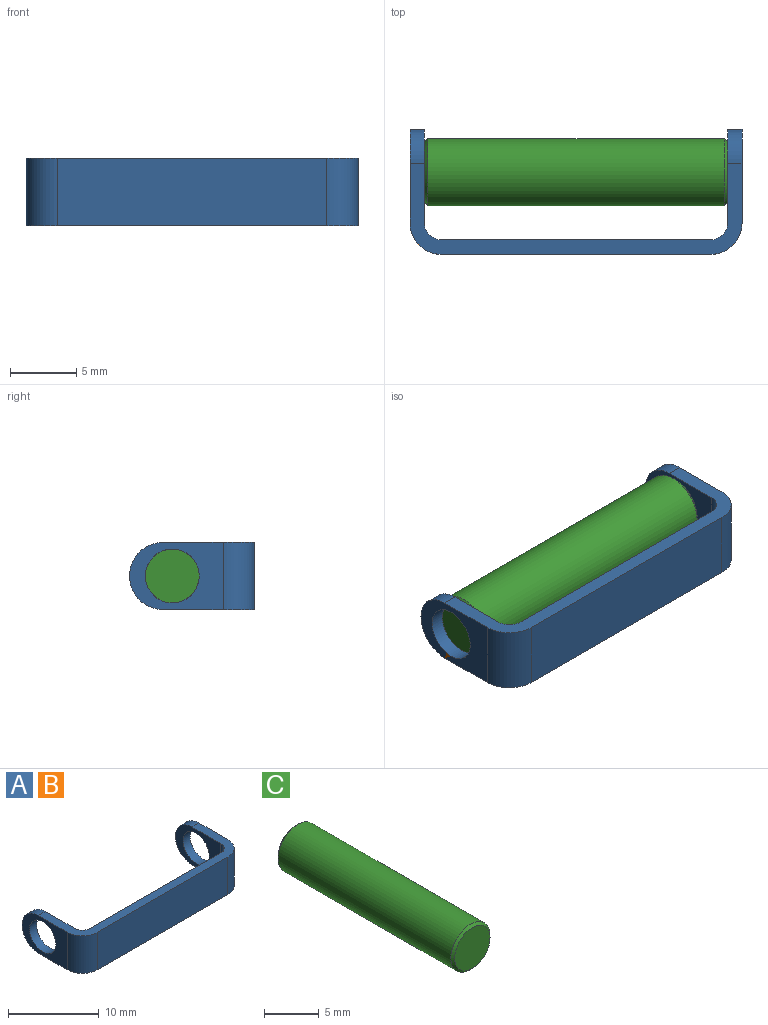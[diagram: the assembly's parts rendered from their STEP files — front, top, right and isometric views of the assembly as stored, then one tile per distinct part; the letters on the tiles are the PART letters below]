
ASSEMBLY  parts=3 mates=1
PART A: 16 faces, bbox 25x9.4x5.1 mm
  f0: cylinder r=1.27mm len=5.08mm, axis (0,0,-1), area 10.1mm2, adj f1,f9,f10,f11
  f1: plane 20.32x5.08mm, normal (0,1,0), area 103.2mm2, adj f0,f2,f10,f11
  f2: cylinder r=1.27mm len=5.08mm, axis (0,0,-1), area 10.1mm2, adj f1,f3,f10,f11
  f3: plane 7.07x5.08mm, normal (1,0,0), area 20.1mm2, adj f2,f10,f11,f13,f15
  f4: plane 7.07x5.08mm, normal (-1,0,0), area 20.1mm2, adj f5,f10,f11,f13,f15
  f5: cylinder r=2.36mm len=5.08mm, axis (0,0,-1), area 18.8mm2, adj f4,f6,f10,f11
  f6: plane 20.32x5.08mm, normal (0,-1,0), area 103.2mm2, adj f5,f7,f10,f11
  f7: cylinder r=2.36mm len=5.08mm, axis (0,0,-1), area 18.8mm2, adj f6,f8,f10,f11
  f8: plane 7.07x5.08mm, normal (1,0,0), area 20.1mm2, adj f7,f10,f11,f12,f14
  f9: plane 7.07x5.08mm, normal (-1,0,0), area 20.1mm2, adj f0,f10,f11,f12,f14
  f10: plane 25.04x6.89mm, normal (0,0,1), area 38.3mm2, adj f0,f1,f2,f3,f4,f5,f6,f7
  f11: plane 25.04x6.89mm, normal (0,0,-1), area 38.3mm2, adj f0,f1,f2,f3,f4,f5,f6,f7
  f12: cylinder r=2.54mm len=5.08mm, axis (1,0,0), area 8.7mm2, adj f8,f9,f10,f11
  f13: cylinder r=2.54mm len=5.08mm, axis (1,0,0), area 8.7mm2, adj f3,f4,f10,f11
  f14: cylinder r=2.03mm len=4.06mm, axis (-1,0,0), area 13.9mm2, adj f8,f9
  f15: cylinder r=2.03mm len=4.06mm, axis (1,0,0), area 13.9mm2, adj f3,f4
PART B: same geometry as A
PART C: 5 faces, bbox 5.1x22.9x5.1 mm
  f0: cylinder r=2.54mm len=22.35mm, axis (0,1,0), area 356.7mm2, adj f3,f4
  f1: plane 4.57x4.57mm, normal (0,-1,0), area 16.4mm2, adj f4
  f2: plane 4.57x4.57mm, normal (0,1,0), area 16.4mm2, adj f3
  f3: cone r=2.54mm half-angle=45deg, axis (0,-1,0), area 5.4mm2, adj f0,f2
  f4: cone r=2.29mm half-angle=45deg, axis (0,1,0), area 5.4mm2, adj f0,f1
PLACE A t=(0.16,-2.74,2.96)mm fixed
PLACE B t=(0.16,-2.74,2.96)mm
PLACE C rot(axis=(-0.58,0.58,0.58),120deg) t=(-11.27,3.46,2.96)mm
MATE fastened C.f0 <-> A.f14  axis (-1,0,0) through (-11.27,3.46,2.96)mm
